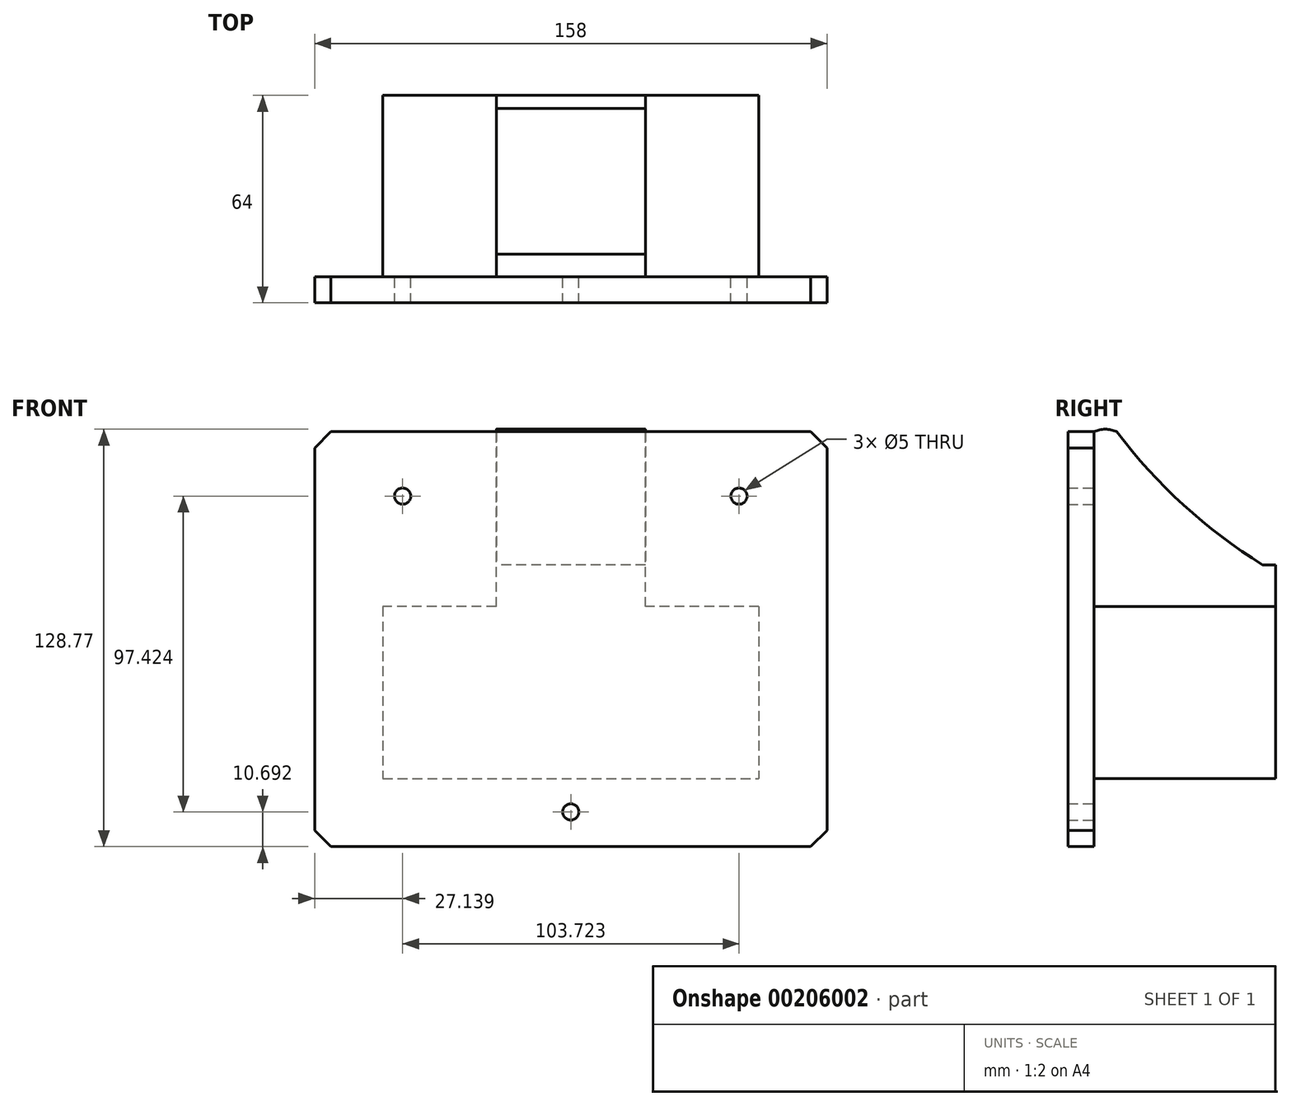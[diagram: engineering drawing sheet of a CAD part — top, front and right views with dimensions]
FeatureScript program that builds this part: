
annotation { "Feature Type Name" : "Feature", "Feature Type Description" : "" }
export const myFeature = defineFeature(function(context is Context, id is Id, definition is map)
    precondition{}
    {
        {
            var Q0;
            Q0=qCreatedBy(makeId("Front.planeOp"),FACE);
            var sketch = newSketch(context, id + "F0", { "sketchPlane" : qUnion([Q0])});
            skPoint(sketch, "E0.middle", {"position": v(0, 0) * mm});
            skLineSegment(sketch, "E1.top", {"start": v(58, 35) * mm, "end": v(-58, 35) * mm});
            skLineSegment(sketch, "E2", {"start": v(58, 35) * mm, "end": v(58, -18) * mm});
            skLineSegment(sketch, "E3", {"start": v(-58, 35) * mm, "end": v(-58, -18) * mm});
            skLineSegment(sketch, "E4", {"start": v(-58, -18) * mm, "end": v(58, -18) * mm});
            skSolve(sketch);
        }
        {
            var Q0;
            Q0=makeQuery(id+"F0.imprint","IMPRINT",FACE,{"disambiguationData":[TD([[makeQuery(id+"F0.imprint","IMPRINT",EDGE,{"derivedFrom":sQuery(id+"F0.wireOp",EDGE,"E1.top")}),1.0]])]});
            extrude(context, id + "F1", {"entities" : qUnion([Q0]), "depth" : 52 * mm});
        }
        {
            var Q0;
            Q0=qCreatedBy(makeId("Right.planeOp"),FACE);
            var sketch = newSketch(context, id + "F2", { "sketchPlane" : qUnion([Q0])});
            skLineSegment(sketch, "E5", {"start": v(0, 0) * mm, "end": v(0, 19) * mm});
            skLineSegment(sketch, "E6", {"start": v(0, 0) * mm, "end": v(-52, 0) * mm});
            skLineSegment(sketch, "E7", {"start": v(-52, 0) * mm, "end": v(-52, 19) * mm});
            skLineSegment(sketch, "E8", {"start": v(-52, 19) * mm, "end": v(-52, 89) * mm});
            skLineSegment(sketch, "E9", {"start": v(0, 19) * mm, "end": v(0, 47.91) * mm});
            skLineSegment(sketch, "E10", {"start": v(-52, 19) * mm, "end": v(-45, 19) * mm});
            skLineSegment(sketch, "E11", {"start": v(-45, 19) * mm, "end": v(-45, 89) * mm});
            skArc(sketch, "E12", {"start": v(-45, 89) * mm, "mid": v(-48.5, 89.77) * mm, "end": v(-52, 89) * mm});
            skArc(sketch, "E13", {"start": v(-45, 89) * mm, "mid": v(-24.38, 66.4) * mm, "end": v(0, 47.91) * mm});
            skPoint(sketch, "E14", {"position": v(0, 35) * mm});
            skLineSegment(sketch, "E15", {"start": v(0, 35) * mm, "end": v(-52, 35) * mm});
            skSolve(sketch);
        }
        {
            var Q0;
            {var subQ0=sQuery(id+"F2.wireOp",EDGE,"E13");Q0=makeQuery(id+"F2.imprint","IMPRINT",FACE,{"disambiguationData":[TD([[makeQuery(id+"F2.imprint","IMPRINT",EDGE,{"derivedFrom":subQ0}),-1.0]])]});}
            var Q1;
            {var subQ0=sQuery(id+"F2.wireOp",EDGE,"E12");Q1=makeQuery(id+"F2.imprint","IMPRINT",FACE,{"disambiguationData":[TD([[makeQuery(id+"F2.imprint","IMPRINT",EDGE,{"derivedFrom":subQ0}),1.0]])]});}
            extrude(context, id + "F3", {"entities" : qUnion([Q0, Q1]), "operationType" : NewBodyOperationType.ADD, "endBound" : BoundingType.SYMMETRIC, "depth" : 46 * mm});
        }
        {
            var Q0;
            Q0=makeQuery(id+"F1.opExtrude","CAP_FACE",FACE,{"disambiguationData":[OSD([sQuery(id+"F0.wireOp",EDGE,"E1.top"),sQuery(id+"F0.wireOp",EDGE,"E2"),sQuery(id+"F0.wireOp",EDGE,"E3"),sQuery(id+"F0.wireOp",EDGE,"E4")])],"isStart":false});
            var sketch = newSketch(context, id + "F4", { "sketchPlane" : qUnion([Q0])});
            skPoint(sketch, "E16", {"position": v(-79, 89) * mm});
            skPoint(sketch, "E17", {"position": v(79, -39) * mm});
            skPoint(sketch, "E18", {"position": v(81, 89) * mm});
            skLineSegment(sketch, "E19.bottom", {"start": v(-79, 89) * mm, "end": v(79, 89) * mm});
            skLineSegment(sketch, "E19.top", {"start": v(-79, -39) * mm, "end": v(79, -39) * mm});
            skLineSegment(sketch, "E19.left", {"start": v(-79, 89) * mm, "end": v(-79, -39) * mm});
            skLineSegment(sketch, "E19.right", {"start": v(79, 89) * mm, "end": v(79, -39) * mm});
            skPoint(sketch, "E20", {"position": v(-51.86, 69.12) * mm});
            skPoint(sketch, "E21", {"position": v(51.86, 69.12) * mm});
            skPoint(sketch, "E22", {"position": v(0, -28.3) * mm});
            skCircle(sketch, "E23", {"center": v(-51.86, 69.12) * mm, "radius": 2.5 * mm});
            skCircle(sketch, "E24.MirrorC", {"center": v(51.86, 69.12) * mm, "radius": 2.5 * mm});
            skCircle(sketch, "E25", {"center": v(0, -28.3) * mm, "radius": 2.5 * mm});
            skSolve(sketch);
        }
        {
            var Q0;
            {var subQ7=sQuery(id+"F4.wireOp",EDGE,"AZ0bNV27-Wc8M-wKK1-qpek-qilTv2k3IYfr.left");Q0=makeQuery(id+"F4.imprint","IMPRINT",FACE,{"disambiguationData":[TD([[makeQuery(id+"F4.imprint","IMPRINT",EDGE,{"derivedFrom":subQ7}),1.0]])]});}
            var Q1;
            {var subQ1=sQuery(id+"F0.wireOp",EDGE,"E0.top");Q1=makeQuery(id+"F4.imprint","IMPRINT",FACE,{"disambiguationData":[TD([[makeQuery(id+"F4.imprint","IMPRINT",EDGE,{"derivedFrom":makeQuery(id+"F1.opExtrude","CAP_EDGE",EDGE,{"disambiguationData":[OSD([subQ1])],"isStart":false})}),1.0]])]});}
            var Q2;
            Q2=makeQuery(id+"F4.imprint","IMPRINT",FACE,{"disambiguationData":[TD([[makeQuery(id+"F4.imprint","IMPRINT",EDGE,{"derivedFrom":sQuery(id+"F4.wireOp",EDGE,"E19.top")}),1.0]])]});
            var Q3;
            Q3=makeQuery(id+"F4.imprint","IMPRINT",FACE,{"disambiguationData":[TD([[makeQuery(id+"F4.imprint","IMPRINT",EDGE,{"derivedFrom":makeQuery(id+"F1.opExtrude","CAP_EDGE",EDGE,{"disambiguationData":[OSD([sQuery(id+"F0.wireOp",EDGE,"E1.top")])],"isStart":false})}),1.0]])]});
            extrude(context, id + "F5", {"entities" : qUnion([Q0, Q1, Q2, Q3]), "operationType" : NewBodyOperationType.ADD, "depth" : 8 * mm});
        }
        {
            var Q0;
            Q0=makeQuery(id+"F5.opExtrude","SWEPT_EDGE",EDGE,{"disambiguationData":[OSD([sQuery(id+"F4.wireOp",EDGE,"E19.bottom"),sQuery(id+"F4.wireOp",EDGE,"E19.left")])]});
            var Q1;
            Q1=makeQuery(id+"F5.opExtrude","SWEPT_EDGE",EDGE,{"disambiguationData":[OSD([sQuery(id+"F4.wireOp",EDGE,"E19.bottom"),sQuery(id+"F4.wireOp",EDGE,"E19.right")])]});
            var Q2;
            Q2=makeQuery(id+"F5.opExtrude","SWEPT_EDGE",EDGE,{"disambiguationData":[OSD([sQuery(id+"F4.wireOp",EDGE,"E19.top"),sQuery(id+"F4.wireOp",EDGE,"E19.right")])]});
            var Q3;
            Q3=makeQuery(id+"F5.opExtrude","SWEPT_EDGE",EDGE,{"disambiguationData":[OSD([sQuery(id+"F4.wireOp",EDGE,"E19.top"),sQuery(id+"F4.wireOp",EDGE,"E19.left")])]});
            chamfer(context, id + "F6", {"entities" : qUnion([Q0, Q1, Q2, Q3]), "width" : 5 * mm, "tangentPropagation" : true});
        }
        {
            var Q0;
            Q0=makeQuery(id+"F3.boolean.opBoolean","MERGE",FACE,{"derivedFrom":[makeQuery(id+"F1.opExtrude","CAP_FACE",FACE,{"disambiguationData":[OSD([sQuery(id+"F0.wireOp",EDGE,"E1.top"),sQuery(id+"F0.wireOp",EDGE,"E2"),sQuery(id+"F0.wireOp",EDGE,"E3"),sQuery(id+"F0.wireOp",EDGE,"E4")])],"isStart":true}),makeQuery(id+"F3.opExtrude","SWEPT_FACE",FACE,{"disambiguationData":[OSD([sQuery(id+"F2.wireOp",EDGE,"E9")])]})]});
            var sketch = newSketch(context, id + "F7", { "sketchPlane" : qUnion([Q0])});
            skLineSegment(sketch, "E26.bottom", {"start": v(-58, 35) * mm, "end": v(58, 35) * mm});
            skLineSegment(sketch, "E26.top", {"start": v(-58, -18) * mm, "end": v(58, -18) * mm});
            skLineSegment(sketch, "E26.left", {"start": v(-58, 35) * mm, "end": v(-58, -18) * mm});
            skLineSegment(sketch, "E26.right", {"start": v(58, 35) * mm, "end": v(58, -18) * mm});
            skLineSegment(sketch, "E27.bottom", {"start": v(-23, 47.91) * mm, "end": v(23, 47.91) * mm});
            skLineSegment(sketch, "E27.top", {"start": v(-23, 35) * mm, "end": v(23, 35) * mm});
            skLineSegment(sketch, "E27.left", {"start": v(-23, 47.91) * mm, "end": v(-23, 35) * mm});
            skLineSegment(sketch, "E27.right", {"start": v(23, 47.91) * mm, "end": v(23, 35) * mm});
            skSolve(sketch);
        }
        {
            var Q0;
            Q0=makeQuery(id+"F7.imprint","IMPRINT",FACE,{"disambiguationData":[TD([[makeQuery(id+"F7.imprint","IMPRINT",EDGE,{"derivedFrom":sQuery(id+"F7.wireOp",EDGE,"E27.bottom")}),-1.0]])]});
            var Q1;
            Q1=makeQuery(id+"F7.imprint","IMPRINT",FACE,{"disambiguationData":[TD([[makeQuery(id+"F7.imprint","IMPRINT",EDGE,{"derivedFrom":sQuery(id+"F7.wireOp",EDGE,"E26.top")}),-1.0]])]});
            extrude(context, id + "F8", {"entities" : qUnion([Q0, Q1]), "operationType" : NewBodyOperationType.ADD, "depth" : 4 * mm});
        }
    });
